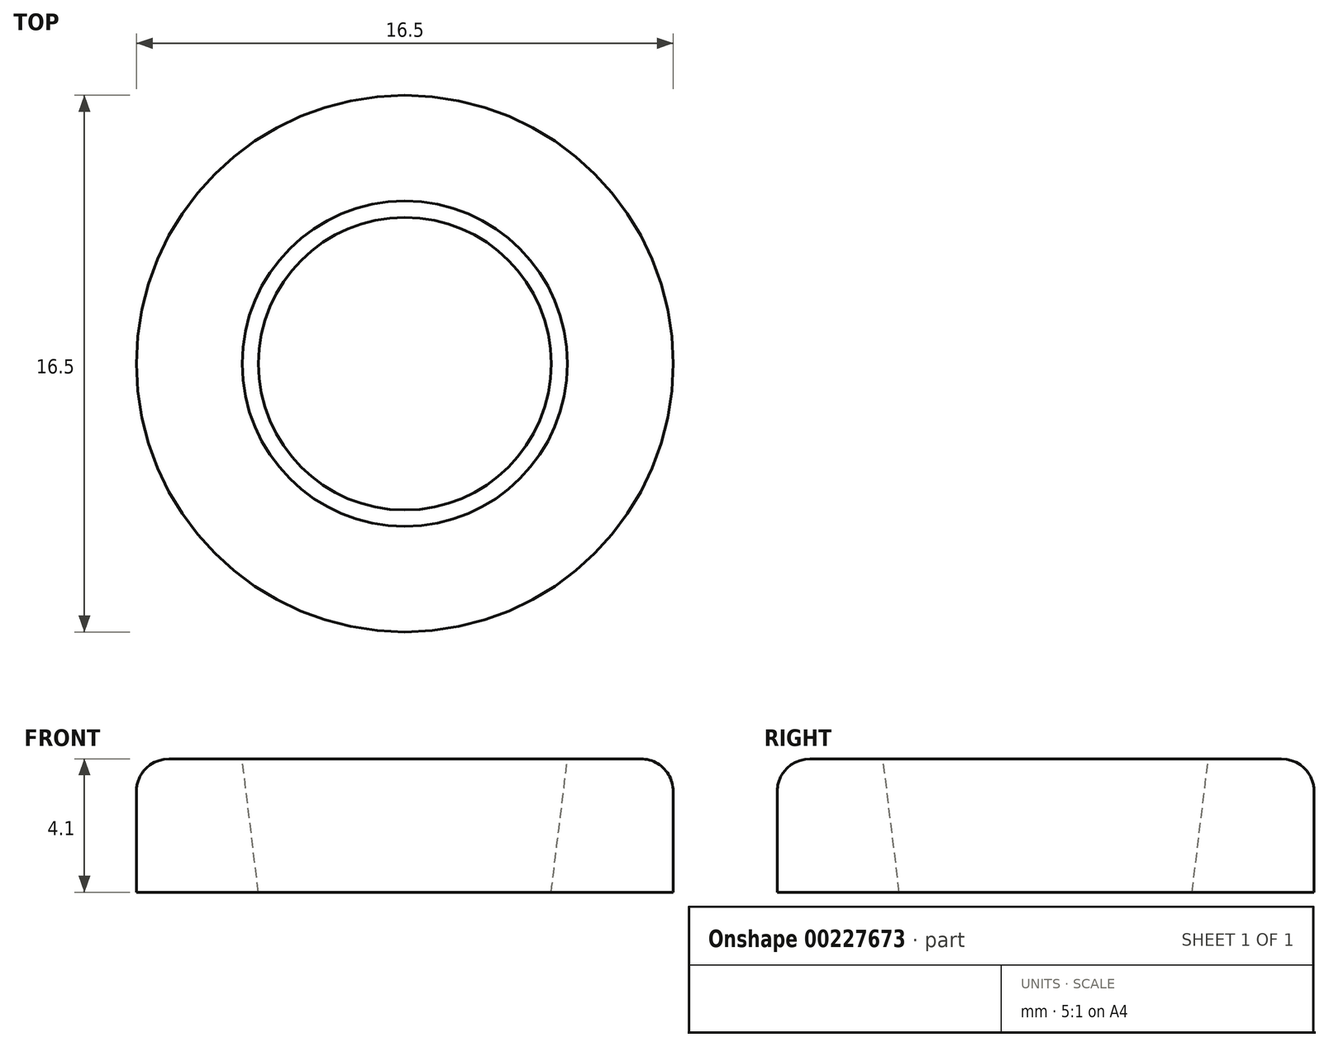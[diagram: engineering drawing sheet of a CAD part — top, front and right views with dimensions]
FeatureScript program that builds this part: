
annotation { "Feature Type Name" : "Feature", "Feature Type Description" : "" }
export const myFeature = defineFeature(function(context is Context, id is Id, definition is map)
    precondition{}
    {
        {
            var Q0;
            Q0=qCreatedBy(makeId("Top.planeOp"),FACE);
            var sketch = newSketch(context, id + "F0", { "sketchPlane" : qUnion([Q0])});
            skCircle(sketch, "E0", {"center": v(0, 0) * mm, "radius": 4.5 * mm});
            skCircle(sketch, "E1", {"center": v(0, 0) * mm, "radius": 8.25 * mm});
            skSolve(sketch);
        }
        {
            var Q0;
            Q0 = qSketchRegion(id + "F0", true);
            extrude(context, id + "F1", {"entities" : qUnion([Q0]), "depth" : 4.1 * mm});
        }
        {
            var Q0;
            Q0=makeQuery(id+"F1.opExtrude","CAP_EDGE",EDGE,{"disambiguationData":[OSD([sQuery(id+"F0.wireOp",EDGE,"E0")])],"isStart":false});
            chamfer(context, id + "F2", {"entities" : qUnion([Q0]), "chamferType" : ChamferType.TWO_OFFSETS, "width1" : 4.1 * mm, "oppositeDirection" : false, "width2" : 0.5 * mm, "tangentPropagation" : true});
        }
        {
            var Q0;
            Q0=makeQuery(id+"F1.opExtrude","CAP_EDGE",EDGE,{"disambiguationData":[OSD([sQuery(id+"F0.wireOp",EDGE,"E1")])],"isStart":false});
            fillet(context, id + "F3", {"entities" : qUnion([Q0]), "radius" : 1 * mm, "tangentPropagation" : true, "allowEdgeOverflow" : false});
        }
    });
